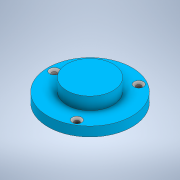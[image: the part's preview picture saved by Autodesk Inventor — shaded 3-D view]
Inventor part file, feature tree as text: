
AUTODESK INVENTOR PART (.ipt)
format: ipt  version: 2021 (Build 250183000, 183)  size: 123,392 bytes
history: native  units: mm
features: sketch x3, extrude x2, hole x1
ambient origin geometry x8: Origin, YZ Plane, XZ Plane, XY Plane, X Axis, Y Axis, Z Axis, Center Point
bodies: Solid1 (feature_tree)
feature tree (6):
  extrude  "Extrusion1"  Depth=4.5mm TaperAngle=0.0deg
  extrude  "Extrusion2"  Depth=6.0mm TaperAngle=0.0deg
  hole  "Hole1"  [1 undecoded]
  sketch  "Sketch1"  dims[d0=40.0mm d1=4.5mm d2=0.0mm]
  sketch  "Sketch2"  dims[d3=22.0mm d4=6.0mm d5=0.0mm]
  sketch  "Sketch3"  dims[d6=34.0mm d7=30.0mm d9=360.0deg d11=2.4mm d12=6.0mm d13=4.4mm d14=2.0mm d15=90.0deg d16=30.0mm d17=20.594885mm]
note: 1 required parameter value undecoded (feature->parameter linkage not recoverable at this tier; creation-order binding heuristic only, values carry confidence <= 0.55)
